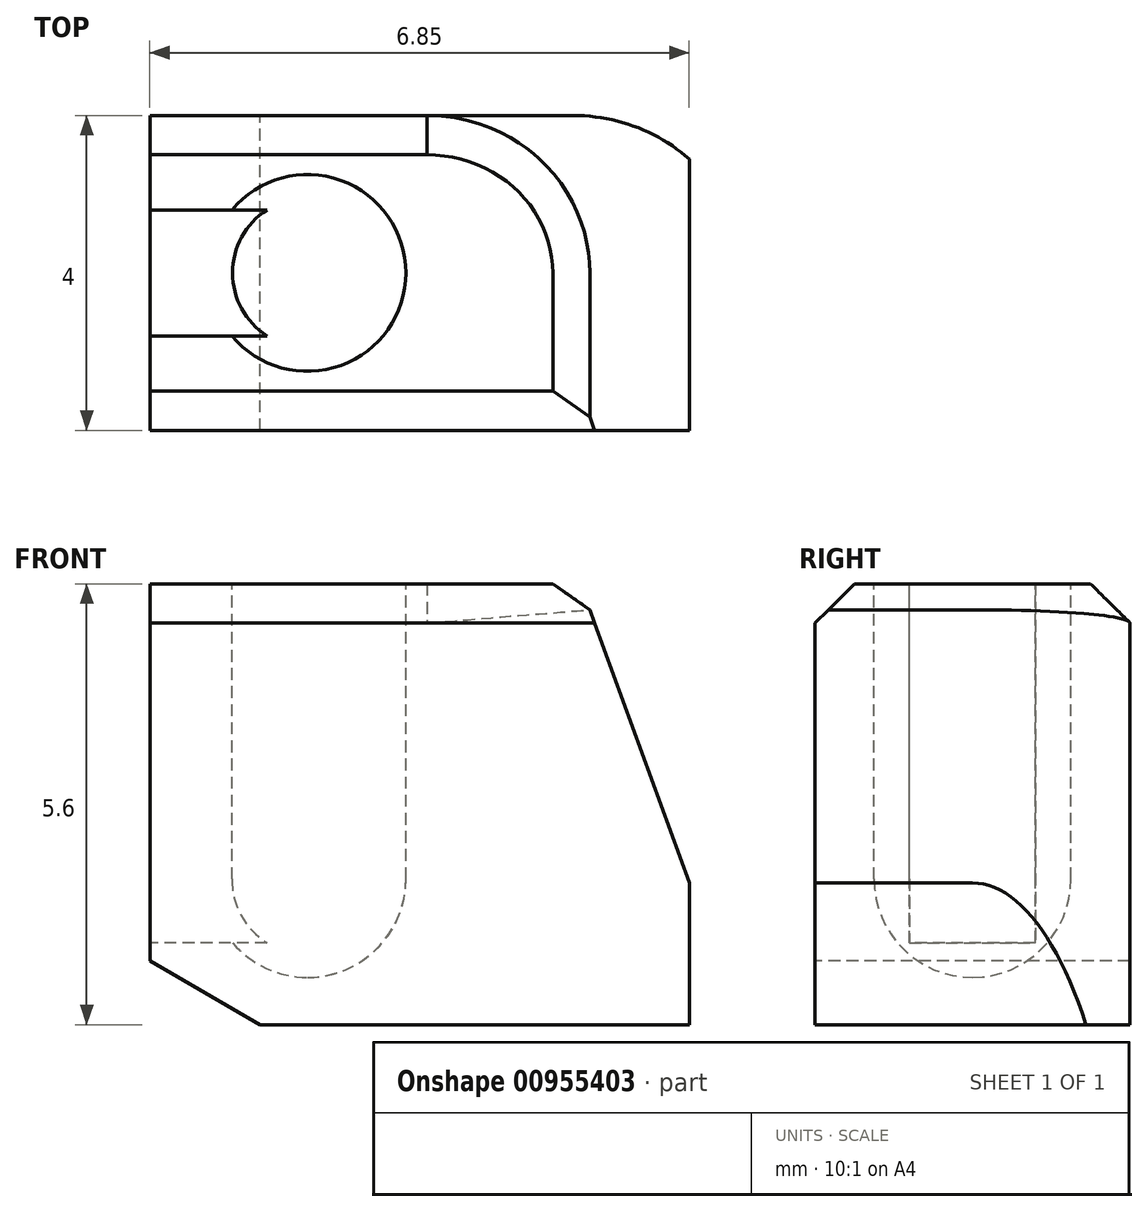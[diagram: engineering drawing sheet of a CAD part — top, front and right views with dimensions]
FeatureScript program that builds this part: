
annotation { "Feature Type Name" : "Feature", "Feature Type Description" : "" }
export const myFeature = defineFeature(function(context is Context, id is Id, definition is map)
    precondition{}
    {
        {
            var Q0;
            Q0=qCreatedBy(makeId("Top.planeOp"),FACE);
            var sketch = newSketch(context, id + "F0", { "sketchPlane" : qUnion([Q0])});
            skLineSegment(sketch, "E0.bottom", {"start": v(4.06, 2) * mm, "end": v(-2.79, 2) * mm});
            skLineSegment(sketch, "E0.top", {"start": v(4.06, -2) * mm, "end": v(-2.79, -2) * mm});
            skLineSegment(sketch, "E0.left", {"start": v(4.06, 2) * mm, "end": v(4.06, -2) * mm});
            skLineSegment(sketch, "E0.right", {"start": v(-2.79, 2) * mm, "end": v(-2.79, -2) * mm});
            skPoint(sketch, "E0.middle", {"position": v(0.64, 0) * mm});
            skSolve(sketch);
        }
        {
            var Q0;
            Q0 = qSketchRegion(id + "F0", true);
            extrude(context, id + "F1", {"entities" : qUnion([Q0]), "depth" : 5.6 * mm, "offsetDistance" : 25 * mm});
        }
        {
            var Q0;
            Q0=makeQuery(id+"F1.opExtrude","SWEPT_FACE",FACE,{"disambiguationData":[OSD([sQuery(id+"F0.wireOp",EDGE,"E0.top")])]});
            var sketch = newSketch(context, id + "F2", { "sketchPlane" : qUnion([Q0])});
            skLineSegment(sketch, "E1", {"start": v(2.68, 5.6) * mm, "end": v(4.06, 1.8) * mm});
            skSolve(sketch);
        }
        {
            var Q0;
            Q0 = qSketchRegion(id + "F2", true);
            var Q1;
            {var subQ0=sQuery(id+"F2.wireOp",EDGE,"E1");Q1=makeQuery(id+"F2.imprint","IMPRINT",FACE,{"disambiguationData":[TD([[makeQuery(id+"F2.imprint","IMPRINT",EDGE,{"derivedFrom":subQ0}),1.0]])]});}
            extrude(context, id + "F3", {"entities" : qUnion([Q0, Q1]), "operationType" : NewBodyOperationType.REMOVE, "oppositeDirection" : true, "depth" : 25 * mm, "offsetDistance" : 25 * mm});
        }
        {
            var Q0;
            Q0=makeQuery(id+"F3.boolean.opBoolean","COPY",EDGE,{"derivedFrom":makeQuery(id+"F3.opExtrude","CAP_EDGE",EDGE,{"disambiguationData":[OSD([sQuery(id+"F2.wireOp",EDGE,"E1")])],"isStart":true})});
            var Q1;
            Q1=makeQuery(id+"F3.boolean.opBoolean","INTERSECT",EDGE,{"derivedFrom":[makeQuery(id+"F1.opExtrude","SWEPT_FACE",FACE,{"disambiguationData":[OSD([sQuery(id+"F0.wireOp",EDGE,"E0.bottom")])]}),makeQuery(id+"F3.opExtrude","SWEPT_FACE",FACE,{"disambiguationData":[OSD([sQuery(id+"F2.wireOp",EDGE,"E1")])]})]});
            fillet(context, id + "F4", {"entities" : qUnion([Q0, Q1]), "tangentPropagation" : true, "radius" : 2 * mm, "defaultsChanged" : true, "vertexSettings" : [], "allowEdgeOverflow" : false});
        }
        {
            var Q0;
            Q0=makeQuery(id+"F1.opExtrude","CAP_EDGE",EDGE,{"disambiguationData":[OSD([sQuery(id+"F0.wireOp",EDGE,"E0.top")])],"isStart":false});
            var Q1;
            {var subQ0=sQuery(id+"F0.wireOp",EDGE,"E0.bottom");Q1=makeQuery(id+"F4.opFillet","BLEND_EDGE",EDGE,{"blendedFrom":[makeQuery(id+"F3.boolean.opBoolean","INTERSECT",EDGE,{"derivedFrom":[makeQuery(id+"F1.opExtrude","SWEPT_FACE",FACE,{"disambiguationData":[OSD([subQ0])]}),makeQuery(id+"F3.opExtrude","SWEPT_FACE",FACE,{"disambiguationData":[OSD([sQuery(id+"F2.wireOp",EDGE,"E1")])]})]}),makeQuery(id+"F1.opExtrude","CAP_FACE",FACE,{"disambiguationData":[OSD([subQ0,sQuery(id+"F0.wireOp",EDGE,"E0.top"),sQuery(id+"F0.wireOp",EDGE,"E0.left"),sQuery(id+"F0.wireOp",EDGE,"E0.right")])],"isStart":false})],"blendedInto":[makeQuery(id+"F1.opExtrude","CAP_FACE",FACE,{"disambiguationData":[OSD([subQ0,sQuery(id+"F0.wireOp",EDGE,"E0.top"),sQuery(id+"F0.wireOp",EDGE,"E0.left"),sQuery(id+"F0.wireOp",EDGE,"E0.right")])],"isStart":false})]});}
            var Q2;
            Q2=makeQuery(id+"F1.opExtrude","CAP_EDGE",EDGE,{"disambiguationData":[OSD([sQuery(id+"F0.wireOp",EDGE,"E0.bottom")])],"isStart":false});
            chamfer(context, id + "F5", {"entities" : qUnion([Q0, Q1, Q2]), "width" : 0.5 * mm, "tangentPropagation" : true});
        }
        {
            var Q0;
            Q0=makeQuery(id+"F1.opExtrude","CAP_EDGE",EDGE,{"disambiguationData":[OSD([sQuery(id+"F0.wireOp",EDGE,"E0.right")])],"isStart":true});
            chamfer(context, id + "F6", {"entities" : qUnion([Q0]), "chamferType" : ChamferType.OFFSET_ANGLE, "width" : 1.4 * mm, "oppositeDirection" : true, "angle" : 30 * degree, "tangentPropagation" : true});
        }
        {
            var Q0;
            Q0=makeQuery(id+"F1.opExtrude","CAP_FACE",FACE,{"disambiguationData":[OSD([sQuery(id+"F0.wireOp",EDGE,"E0.bottom"),sQuery(id+"F0.wireOp",EDGE,"E0.top"),sQuery(id+"F0.wireOp",EDGE,"E0.left"),sQuery(id+"F0.wireOp",EDGE,"E0.right")])],"isStart":false});
            var sketch = newSketch(context, id + "F7", { "sketchPlane" : qUnion([Q0])});
            skCircle(sketch, "E2", {"center": v(-0.79, 0) * mm, "radius": 1.25 * mm});
            skSolve(sketch);
        }
        {
            var Q0;
            Q0 = qSketchRegion(id + "F7", true);
            extrude(context, id + "F8", {"entities" : qUnion([Q0]), "operationType" : NewBodyOperationType.REMOVE, "oppositeDirection" : true, "depth" : 5 * mm, "offsetDistance" : 25 * mm});
        }
        {
            var Q0;
            Q0=makeQuery(id+"F8.boolean.opBoolean","COPY",EDGE,{"derivedFrom":makeQuery(id+"F8.opExtrude","CAP_EDGE",EDGE,{"disambiguationData":[OSD([sQuery(id+"F7.wireOp",EDGE,"E2")])],"isStart":false})});
            fillet(context, id + "F9", {"entities" : qUnion([Q0]), "tangentPropagation" : true, "radius" : 1.25 * mm, "defaultsChanged" : true, "vertexSettings" : [], "allowEdgeOverflow" : false});
        }
        {
            var Q0;
            Q0=makeQuery(id+"F1.opExtrude","SWEPT_FACE",FACE,{"disambiguationData":[OSD([sQuery(id+"F0.wireOp",EDGE,"E0.right")])]});
            var sketch = newSketch(context, id + "F10", { "sketchPlane" : qUnion([Q0])});
            skLineSegment(sketch, "E3", {"start": v(-0.8, 5.6) * mm, "end": v(-0.8, 1.04) * mm});
            skLineSegment(sketch, "E4", {"start": v(-0.8, 1.04) * mm, "end": v(0.8, 1.04) * mm});
            skLineSegment(sketch, "E5", {"start": v(0.8, 1.04) * mm, "end": v(0.8, 5.6) * mm});
            skSolve(sketch);
        }
        {
            var Q0;
            Q0 = qSketchRegion(id + "F10", true);
            var Q1;
            {var subQ0=sQuery(id+"F10.wireOp",EDGE,"E3");Q1=makeQuery(id+"F10.imprint","IMPRINT",FACE,{"disambiguationData":[TD([[makeQuery(id+"F10.imprint","IMPRINT",EDGE,{"derivedFrom":subQ0}),1.0]])]});}
            extrude(context, id + "F11", {"entities" : qUnion([Q0, Q1]), "operationType" : NewBodyOperationType.REMOVE, "oppositeDirection" : true, "depth" : 1.5 * mm, "offsetDistance" : 25 * mm});
        }
    });
